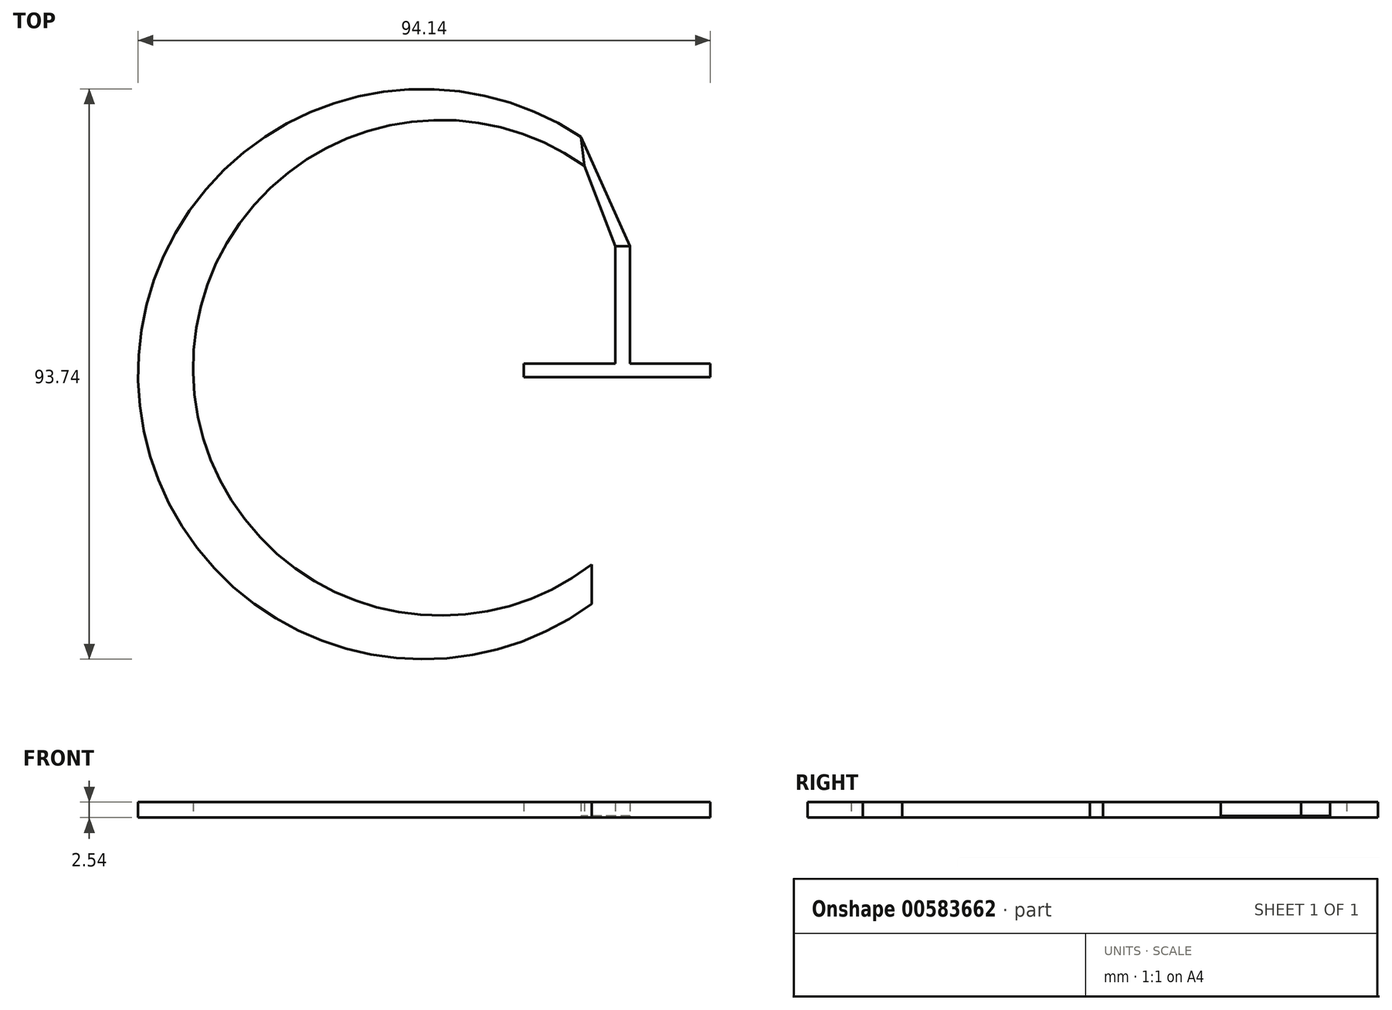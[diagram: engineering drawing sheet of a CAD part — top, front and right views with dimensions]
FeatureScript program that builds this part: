
annotation { "Feature Type Name" : "Feature", "Feature Type Description" : "" }
export const myFeature = defineFeature(function(context is Context, id is Id, definition is map)
    precondition{}
    {
        {
            var Q0;
            Q0=qCreatedBy(makeId("Top.planeOp"),FACE);
            var sketch = newSketch(context, id + "F0", { "sketchPlane" : qUnion([Q0])});
            skArc(sketch, "E0", {"start": v(-12.78, 34.74) * mm, "mid": v(-77.1, 0.76) * mm, "end": v(-11.58, -30.83) * mm});
            skLineSegment(sketch, "E1", {"start": v(-7.67, 21.5) * mm, "end": v(-7.67, -30.83) * mm});
            skLineSegment(sketch, "E2", {"start": v(-7.67, -30.83) * mm, "end": v(-7.67, 0) * mm});
            skLineSegment(sketch, "E3", {"start": v(-7.67, 0) * mm, "end": v(-22.7, 0) * mm});
            skLineSegment(sketch, "E4", {"start": v(-22.7, 0) * mm, "end": v(7.97, 0) * mm});
            skLineSegment(sketch, "E5", {"start": v(-7.67, 21.5) * mm, "end": v(-12.78, 34.74) * mm});
            skLineSegment(sketch, "E6", {"start": v(-7.67, -30.83) * mm, "end": v(-11.58, -30.83) * mm});
            skLineSegment(sketch, "E7", {"start": v(-7.67, -30.83) * mm, "end": v(-5.27, -29.86) * mm});
            skLineSegment(sketch, "E8", {"start": v(-5.27, -29.86) * mm, "end": v(-5.27, 21.5) * mm});
            skLineSegment(sketch, "E9", {"start": v(-5.27, 21.5) * mm, "end": v(-7.67, 21.5) * mm});
            skLineSegment(sketch, "E10", {"start": v(-22.7, 0) * mm, "end": v(-22.7, 2.18) * mm});
            skLineSegment(sketch, "E11", {"start": v(-22.7, 2.18) * mm, "end": v(7.97, 2.18) * mm});
            skLineSegment(sketch, "E12", {"start": v(7.97, 2.18) * mm, "end": v(7.97, 0) * mm});
            skArc(sketch, "E13", {"start": v(-13.3, 39.48) * mm, "mid": v(-86.15, -0.58) * mm, "end": v(-11.58, -37.31) * mm});
            skLineSegment(sketch, "E14", {"start": v(-12.78, 34.74) * mm, "end": v(-13.3, 39.48) * mm});
            skLineSegment(sketch, "E15", {"start": v(-11.58, -30.83) * mm, "end": v(-11.58, -37.31) * mm});
            skLineSegment(sketch, "E16", {"start": v(-5.27, 21.5) * mm, "end": v(-13.3, 39.48) * mm});
            skSolve(sketch);
        }
        {
            var Q0;
            Q0=makeQuery(id+"F0.imprint","IMPRINT",FACE,{"disambiguationData":[TD([[makeQuery(id+"F0.imprint","IMPRINT",EDGE,{"derivedFrom":sQuery(id+"F0.wireOp",EDGE,"E0")}),-1.0]])]});
            var Q1;
            {var subQ0=sQuery(id+"F0.wireOp",EDGE,"E9");Q1=makeQuery(id+"F0.imprint","IMPRINT",FACE,{"disambiguationData":[TD([[makeQuery(id+"F0.imprint","IMPRINT",EDGE,{"derivedFrom":subQ0}),1.0]])]});}
            var Q2;
            {var subQ0=sQuery(id+"F0.wireOp",EDGE,"E2");Q2=makeQuery(id+"F0.imprint","IMPRINT",FACE,{"disambiguationData":[TD([[makeQuery(id+"F0.imprint","IMPRINT",EDGE,{"derivedFrom":subQ0}),-1.0]])]});}
            var Q3;
            {var subQ5=sQuery(id+"F0.wireOp",EDGE,"E10");Q3=makeQuery(id+"F0.imprint","IMPRINT",FACE,{"disambiguationData":[TD([[makeQuery(id+"F0.imprint","IMPRINT",EDGE,{"derivedFrom":subQ5}),-1.0]])]});}
            var Q4;
            {var subQ0=sQuery(id+"F0.wireOp",EDGE,"E12");Q4=makeQuery(id+"F0.imprint","IMPRINT",FACE,{"disambiguationData":[TD([[makeQuery(id+"F0.imprint","IMPRINT",EDGE,{"derivedFrom":subQ0}),-1.0]])]});}
            var Q5;
            {var subQ0=sQuery(id+"F0.wireOp",EDGE,"E4");var subQ5=sQuery(id+"F0.wireOp",EDGE,"E8");var subQ6=makeQuery(id+"F0.imprint","INTERSECT",VERTEX,{"derivedFrom":[subQ0,subQ5]});Q5=makeQuery(id+"F0.imprint","IMPRINT",FACE,{"disambiguationData":[TD([[makeQuery(id+"F0.imprint","IMPRINT",EDGE,{"disambiguationData":[TD([[subQ6,-1.0]])],"derivedFrom":subQ5}),1.0]])]});}
            extrude(context, id + "F1", {"entities" : qUnion([Q0, Q1, Q2, Q3, Q4, Q5]), "depth" : 2.54 * mm, "offsetDistance" : 25.4 * mm});
        }
        {
            var Q0;
            Q0=makeQuery(id+"F0.imprint","IMPRINT",FACE,{"disambiguationData":[TD([[makeQuery(id+"F0.imprint","IMPRINT",EDGE,{"derivedFrom":sQuery(id+"F0.wireOp",EDGE,"E5")}),-1.0]])]});
            extrude(context, id + "F2", {"entities" : qUnion([Q0]), "depth" : 0.25 * mm, "offsetDistance" : 25.4 * mm});
        }
    });
